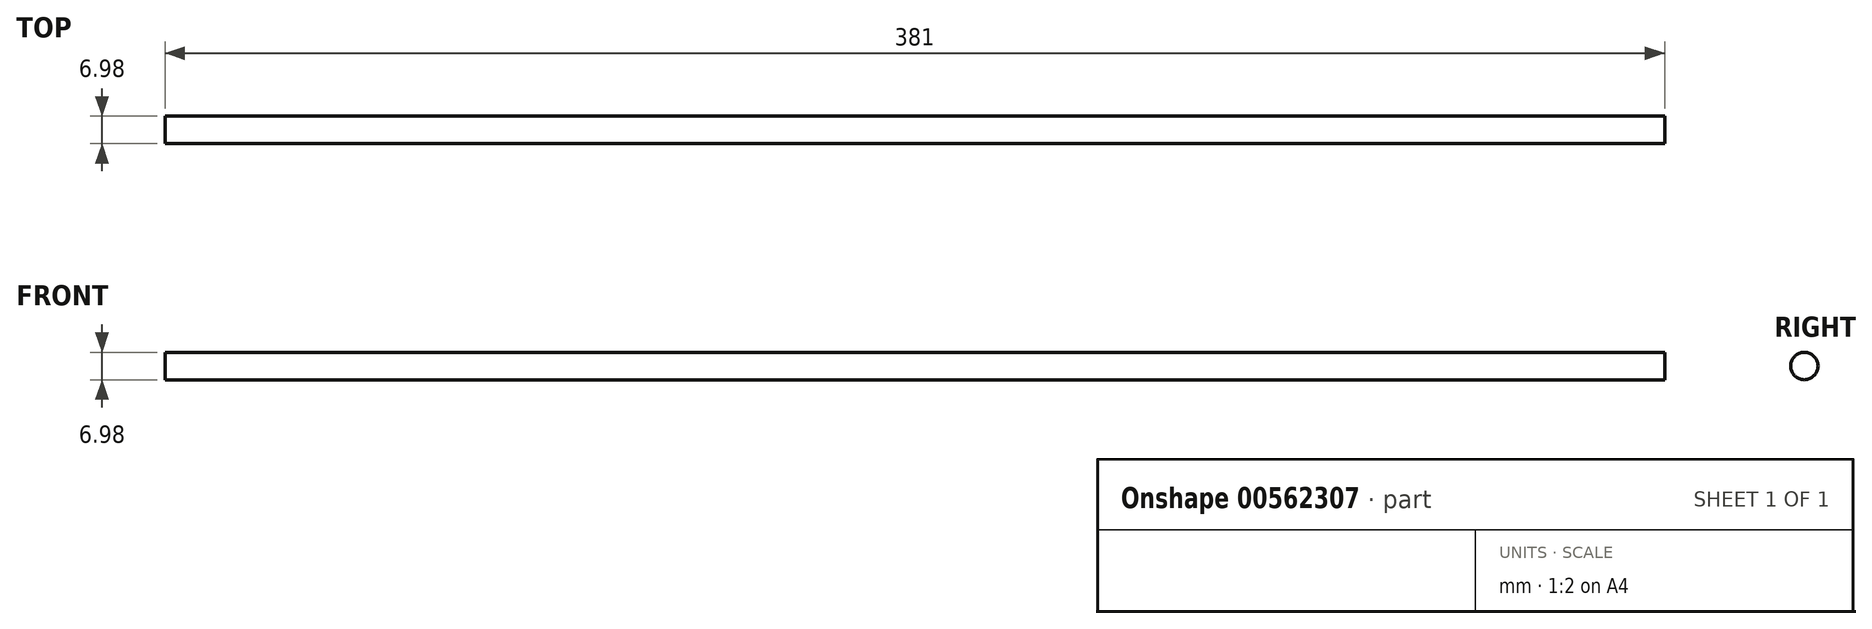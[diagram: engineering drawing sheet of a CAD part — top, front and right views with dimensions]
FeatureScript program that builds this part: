
annotation { "Feature Type Name" : "Feature", "Feature Type Description" : "" }
export const myFeature = defineFeature(function(context is Context, id is Id, definition is map)
    precondition{}
    {
        {
            var Q0;
            Q0=qCreatedBy(makeId("Right.planeOp"),FACE);
            var sketch = newSketch(context, id + "F0", { "sketchPlane" : qUnion([Q0])});
            skCircle(sketch, "E0", {"center": v(0, 0) * mm, "radius": 3.5 * mm});
            skSolve(sketch);
        }
        {
            var Q0;
            Q0=makeQuery(id+"F0.imprint","IMPRINT",FACE,{"disambiguationData":[TD([[makeQuery(id+"F0.imprint","IMPRINT",EDGE,{"derivedFrom":sQuery(id+"F0.wireOp",EDGE,"E0")}),1.0]])]});
            extrude(context, id + "F1", {"entities" : qUnion([Q0]), "depth" : 381 * mm, "offsetDistance" : 25.4 * mm});
        }
    });
